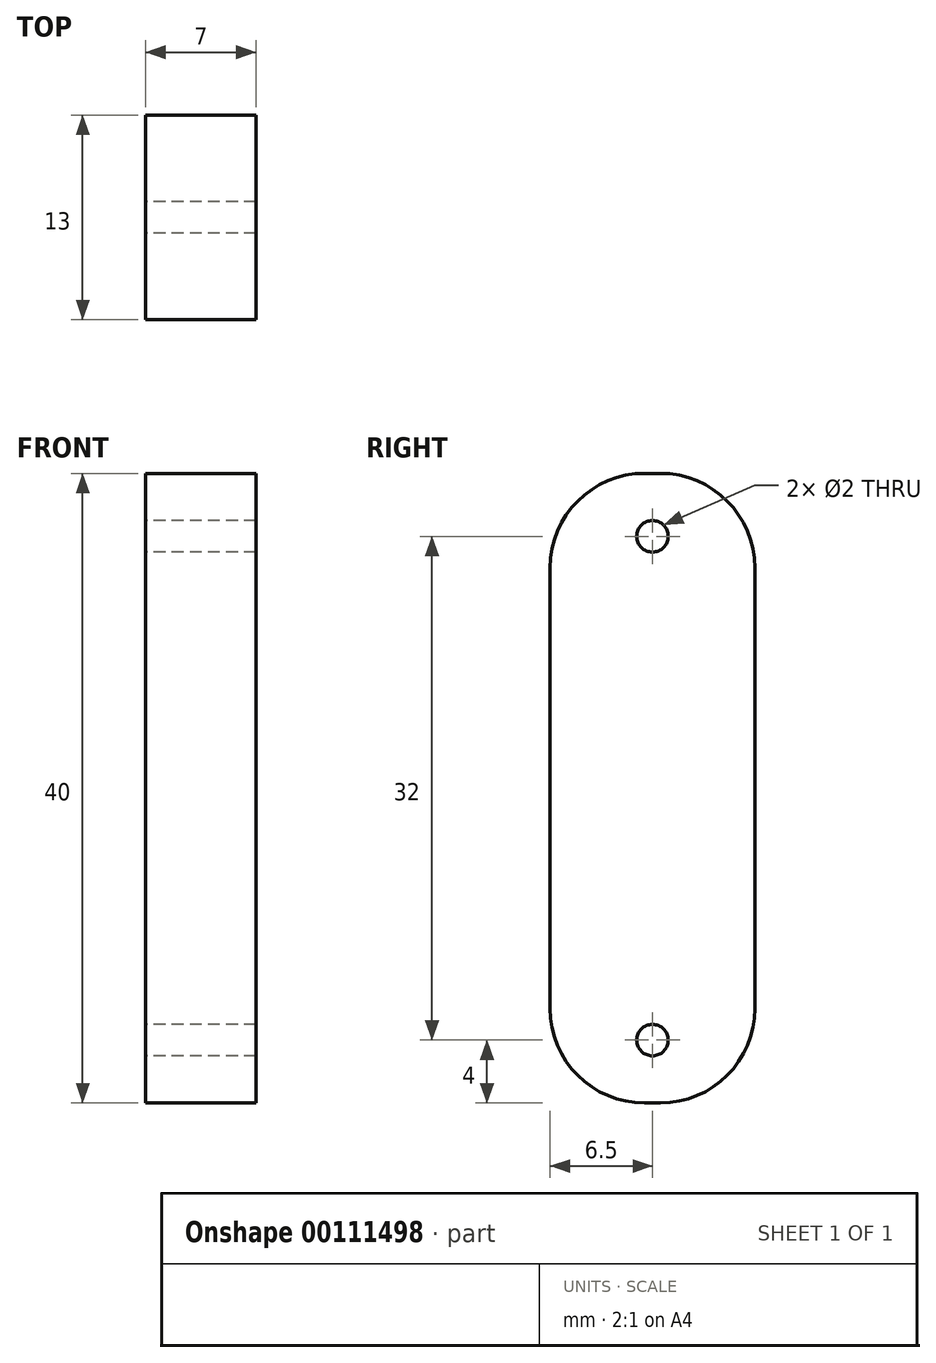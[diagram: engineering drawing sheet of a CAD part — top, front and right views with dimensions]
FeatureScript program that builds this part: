
annotation { "Feature Type Name" : "Feature", "Feature Type Description" : "" }
export const myFeature = defineFeature(function(context is Context, id is Id, definition is map)
    precondition{}
    {
        {
            var Q0;
            Q0=qCreatedBy(makeId("Top.planeOp"),FACE);
            var sketch = newSketch(context, id + "F0", { "sketchPlane" : qUnion([Q0])});
            skLineSegment(sketch, "E0.bottom", {"start": v(3.5, 6.5) * mm, "end": v(-3.5, 6.5) * mm});
            skLineSegment(sketch, "E0.top", {"start": v(3.5, -6.5) * mm, "end": v(-3.5, -6.5) * mm});
            skLineSegment(sketch, "E0.left", {"start": v(3.5, 6.5) * mm, "end": v(3.5, -6.5) * mm});
            skLineSegment(sketch, "E0.right", {"start": v(-3.5, 6.5) * mm, "end": v(-3.5, -6.5) * mm});
            skPoint(sketch, "E0.middle", {"position": v(0, 0) * mm});
            skSolve(sketch);
        }
        {
            var Q0;
            Q0=makeQuery(id+"F0.imprint","IMPRINT",FACE,{"disambiguationData":[TD([[makeQuery(id+"F0.imprint","IMPRINT",EDGE,{"derivedFrom":sQuery(id+"F0.wireOp",EDGE,"E0.bottom")}),1.0]])]});
            extrude(context, id + "F1", {"entities" : qUnion([Q0]), "depth" : 40 * mm});
        }
        {
            var Q0;
            Q0=makeQuery(id+"F1.opExtrude","CAP_EDGE",EDGE,{"disambiguationData":[OSD([sQuery(id+"F0.wireOp",EDGE,"E0.bottom")])],"isStart":false});
            var Q1;
            Q1=makeQuery(id+"F1.opExtrude","CAP_EDGE",EDGE,{"disambiguationData":[OSD([sQuery(id+"F0.wireOp",EDGE,"E0.top")])],"isStart":false});
            var Q2;
            Q2=makeQuery(id+"F1.opExtrude","CAP_EDGE",EDGE,{"disambiguationData":[OSD([sQuery(id+"F0.wireOp",EDGE,"E0.bottom")])],"isStart":true});
            var Q3;
            Q3=makeQuery(id+"F1.opExtrude","CAP_EDGE",EDGE,{"disambiguationData":[OSD([sQuery(id+"F0.wireOp",EDGE,"E0.top")])],"isStart":true});
            fillet(context, id + "F2", {"entities" : qUnion([Q0, Q1, Q2, Q3]), "radius" : 6 * mm, "tangentPropagation" : true, "allowEdgeOverflow" : false});
        }
        {
            var Q0;
            Q0=makeQuery(id+"F1.opExtrude","SWEPT_FACE",FACE,{"disambiguationData":[OSD([sQuery(id+"F0.wireOp",EDGE,"E0.right")])]});
            var sketch = newSketch(context, id + "F3", { "sketchPlane" : qUnion([Q0])});
            skPoint(sketch, "E1", {"position": v(0, 36) * mm});
            skSolve(sketch);
        }
        {
            var Q0;
            {var subQ0=sQuery(id+"F0.wireOp",EDGE,"E0.right");Q0=makeQuery(id+"F3.imprint","IMPRINT",FACE,{"disambiguationData":[TD([[makeQuery(id+"F3.imprint","IMPRINT",EDGE,{"derivedFrom":makeQuery(id+"F1.opExtrude","CAP_EDGE",EDGE,{"disambiguationData":[OSD([subQ0])],"isStart":true})}),1.0]])]});}
            var sketch = newSketch(context, id + "F4", { "sketchPlane" : qUnion([Q0])});
            skPoint(sketch, "E2", {"position": v(0, 4) * mm});
            skSolve(sketch);
        }
        {
            var Q0;
            Q0=sQuery(id+"F4.wireOp",VERTEX,"E2");
            var Q1;
            Q1=sQuery(id+"F3.wireOp",VERTEX,"E1");
            var Q2;
            Q2=makeQuery(id+"F1.opExtrude","SWEPT_BODY",BODY,{"disambiguationData":[OSD([sQuery(id+"F0.wireOp",EDGE,"E0.bottom"),sQuery(id+"F0.wireOp",EDGE,"E0.top"),sQuery(id+"F0.wireOp",EDGE,"E0.left"),sQuery(id+"F0.wireOp",EDGE,"E0.right")])]});
            hole(context, id + "F5", {"style" : HoleStyle.SIMPLE, "endStyle" : HoleEndStyle.THROUGH, "holeDiameter" : 2 * mm, "locations" : qUnion([Q0, Q1]), "scope" : qUnion([Q2]), "isTappedThrough" : true});
        }
    });
